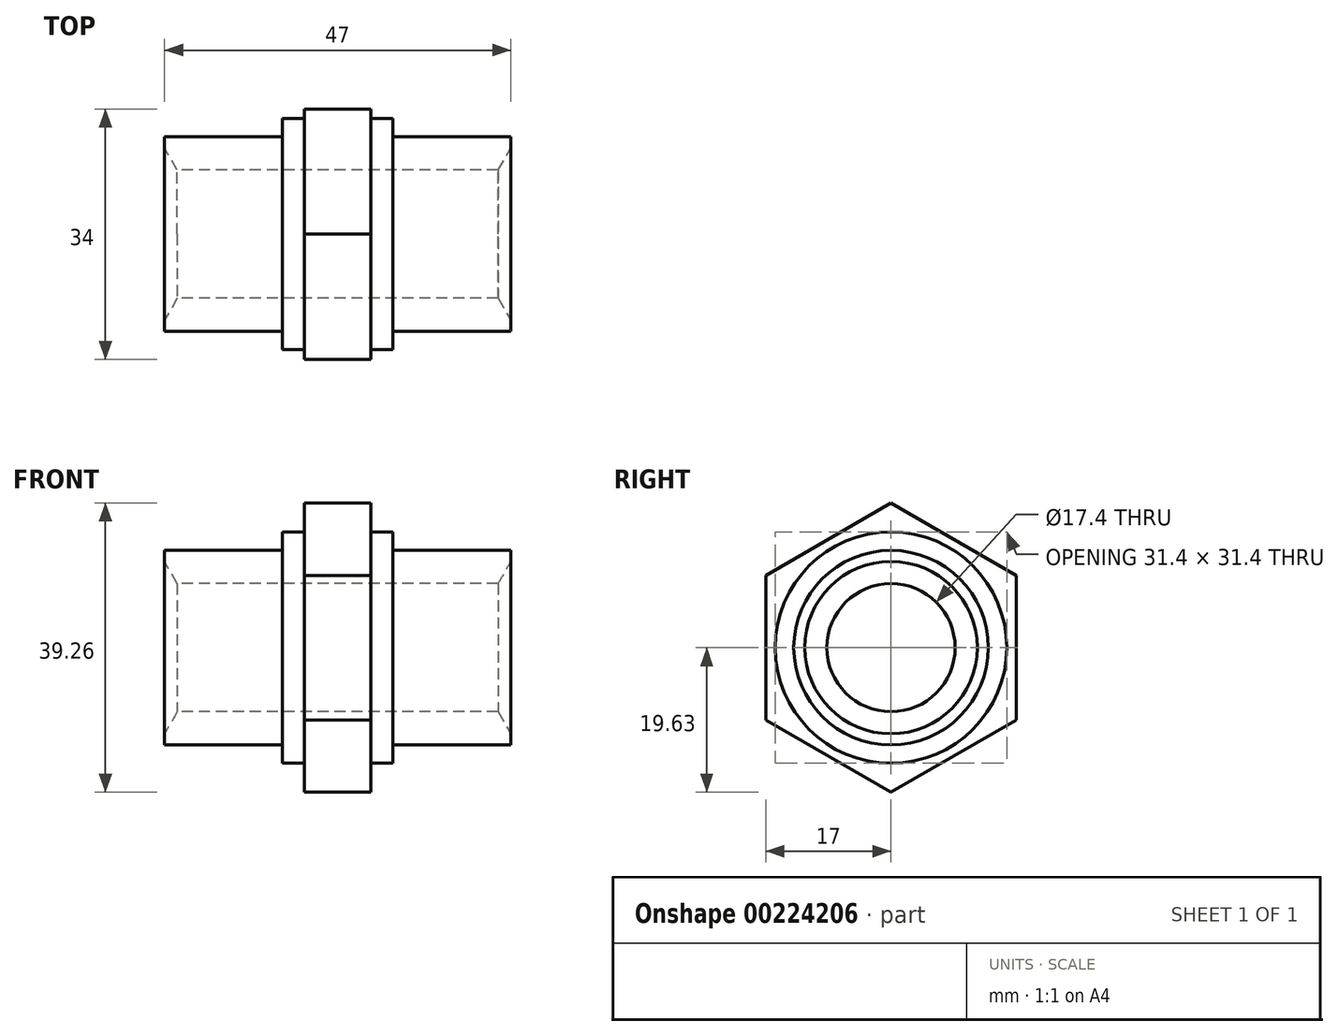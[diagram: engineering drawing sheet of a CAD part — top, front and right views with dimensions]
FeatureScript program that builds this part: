
annotation { "Feature Type Name" : "Feature", "Feature Type Description" : "" }
export const myFeature = defineFeature(function(context is Context, id is Id, definition is map)
    precondition{}
    {
        {
            var Q0;
            Q0=qCreatedBy(makeId("Front.planeOp"),FACE);
            var sketch = newSketch(context, id + "F0", { "sketchPlane" : qUnion([Q0])});
            skLineSegment(sketch, "E0", {"start": v(-23.5, 0) * mm, "end": v(0, 0) * mm, "construction": true});
            skLineSegment(sketch, "E1", {"start": v(0, 0) * mm, "end": v(23.5, 0) * mm, "construction": true});
            skLineSegment(sketch, "E2", {"start": v(23.5, 8.7) * mm, "end": v(23.5, 13.2) * mm});
            skLineSegment(sketch, "E3", {"start": v(23.5, 13.2) * mm, "end": v(7.5, 13.2) * mm});
            skLineSegment(sketch, "E4", {"start": v(7.5, 13.2) * mm, "end": v(7.5, 15.7) * mm});
            skLineSegment(sketch, "E5", {"start": v(7.5, 15.7) * mm, "end": v(-7.5, 15.7) * mm});
            skLineSegment(sketch, "E6", {"start": v(-7.5, 15.7) * mm, "end": v(-7.5, 13.2) * mm});
            skLineSegment(sketch, "E7", {"start": v(-7.5, 13.2) * mm, "end": v(-23.5, 13.2) * mm});
            skLineSegment(sketch, "E8", {"start": v(-23.5, 13.2) * mm, "end": v(-23.5, 8.7) * mm});
            skLineSegment(sketch, "E9", {"start": v(-34.49, 0) * mm, "end": v(-23.5, 0) * mm, "construction": true});
            skPoint(sketch, "E9.endSnap0", {"position": v(11.75, 0) * mm});
            skLineSegment(sketch, "E10", {"start": v(-23.5, 8.7) * mm, "end": v(23.5, 8.7) * mm});
            skLineSegment(sketch, "E11.trimOffspring", {"start": v(23.5, 0) * mm, "end": v(41.66, 0) * mm, "construction": true});
            skSolve(sketch);
        }
        {
            var Q0;
            Q0=makeQuery(id+"F0.imprint","IMPRINT",FACE,{"disambiguationData":[TD([[makeQuery(id+"F0.imprint","IMPRINT",EDGE,{"derivedFrom":sQuery(id+"F0.wireOp",EDGE,"E2")}),1.0]])]});
            var Q1;
            Q1=sQuery(id+"F0.wireOp",EDGE,"E0");
            revolve(context, id + "F1", {"entities" : qUnion([Q0]), "axis" : qUnion([Q1]), "revolveType" : RevolveType.FULL});
        }
        {
            var Q0;
            Q0=makeQuery(id+"F1.opRevolve","SWEPT_EDGE",EDGE,{"disambiguationData":[OSD([sQuery(id+"F0.wireOp",EDGE,"E2"),sQuery(id+"F0.wireOp",EDGE,"E10")])]});
            var Q1;
            Q1=makeQuery(id+"F1.opRevolve","SWEPT_EDGE",EDGE,{"disambiguationData":[OSD([sQuery(id+"F0.wireOp",EDGE,"E8"),sQuery(id+"F0.wireOp",EDGE,"E10")])]});
            chamfer(context, id + "F2", {"entities" : qUnion([Q0, Q1]), "chamferType" : ChamferType.OFFSET_ANGLE, "width" : 3 * mm, "oppositeDirection" : false, "angle" : 30 * degree, "tangentPropagation" : true});
        }
        {
            var Q0;
            Q0=qCreatedBy(makeId("Right.planeOp"),FACE);
            var sketch = newSketch(context, id + "F3", { "sketchPlane" : qUnion([Q0])});
            skCircle(sketch, "E12.cCircle", {"center": v(0, 0) * mm, "radius": 17 * mm, "construction": true});
            skLineSegment(sketch, "E12.0", {"start": v(17, 9.81) * mm, "end": v(17, -9.81) * mm});
            skLineSegment(sketch, "E12.1", {"start": v(17, -9.81) * mm, "end": v(0, -19.63) * mm});
            skLineSegment(sketch, "E12.2", {"start": v(0, -19.63) * mm, "end": v(-17, -9.81) * mm});
            skLineSegment(sketch, "E12.3", {"start": v(-17, -9.81) * mm, "end": v(-17, 9.81) * mm});
            skLineSegment(sketch, "E12.4", {"start": v(-17, 9.81) * mm, "end": v(0, 19.63) * mm});
            skLineSegment(sketch, "E12.5", {"start": v(0, 19.63) * mm, "end": v(17, 9.81) * mm});
            skPoint(sketch, "E12.0.midPoint", {"position": v(17, 0) * mm});
            skCircle(sketch, "E13", {"center": v(0, 0) * mm, "radius": 8.7 * mm});
            skSolve(sketch);
        }
        {
            var Q0;
            Q0 = qSketchRegion(id + "F3", true);
            extrude(context, id + "F4", {"entities" : qUnion([Q0]), "operationType" : NewBodyOperationType.ADD, "endBound" : BoundingType.SYMMETRIC, "depth" : 9 * mm});
        }
    });
